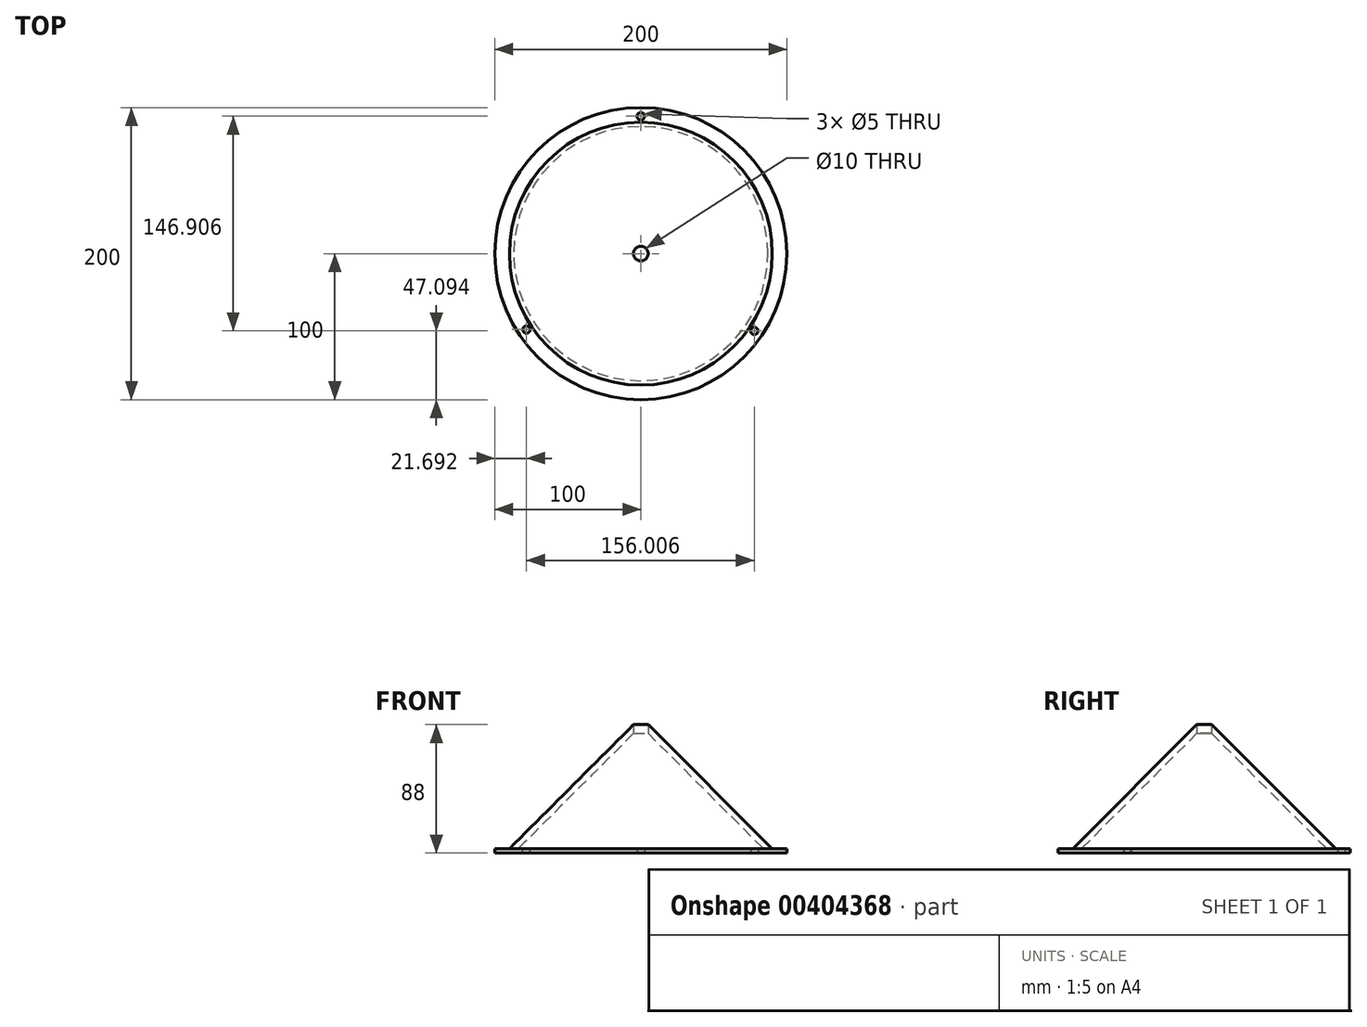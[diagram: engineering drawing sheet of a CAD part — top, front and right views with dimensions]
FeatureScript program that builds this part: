
annotation { "Feature Type Name" : "Feature", "Feature Type Description" : "" }
export const myFeature = defineFeature(function(context is Context, id is Id, definition is map)
    precondition{}
    {
        {
            var Q0;
            Q0=qCreatedBy(makeId("Front.planeOp"),FACE);
            var sketch = newSketch(context, id + "F0", { "sketchPlane" : qUnion([Q0])});
            skLineSegment(sketch, "E0", {"start": v(0, 0) * mm, "end": v(-100, 0) * mm});
            skLineSegment(sketch, "E1", {"start": v(-100, 0) * mm, "end": v(-100, 3) * mm});
            skLineSegment(sketch, "E2", {"start": v(-100, 3) * mm, "end": v(-90, 3) * mm});
            skLineSegment(sketch, "E3", {"start": v(-90, 3) * mm, "end": v(0, 93) * mm});
            skLineSegment(sketch, "E4", {"start": v(0, 93) * mm, "end": v(0, 0) * mm});
            skSolve(sketch);
        }
        {
            var Q0;
            Q0=makeQuery(id+"F0.imprint","IMPRINT",FACE,{"disambiguationData":[TD([[makeQuery(id+"F0.imprint","IMPRINT",EDGE,{"derivedFrom":sQuery(id+"F0.wireOp",EDGE,"E0")}),-1.0]])]});
            var Q1;
            Q1=sQuery(id+"F0.wireOp",EDGE,"E4");
            revolve(context, id + "F1", {"entities" : qUnion([Q0]), "axis" : qUnion([Q1]), "revolveType" : RevolveType.FULL});
        }
        {
            var Q0;
            Q0=makeQuery(id+"F1.opRevolve","SWEPT_FACE",FACE,{"disambiguationData":[OSD([sQuery(id+"F0.wireOp",EDGE,"E0")])]});
            var sketch = newSketch(context, id + "F2", { "sketchPlane" : qUnion([Q0])});
            skCircle(sketch, "E5", {"center": v(0, 0) * mm, "radius": 87 * mm});
            skSolve(sketch);
        }
        {
            var Q0;
            Q0=makeQuery(id+"F2.imprint","IMPRINT",FACE,{"disambiguationData":[TD([[makeQuery(id+"F2.imprint","IMPRINT",EDGE,{"derivedFrom":sQuery(id+"F2.wireOp",EDGE,"E5")}),1.0]])]});
            extrude(context, id + "F3", {"entities" : qUnion([Q0]), "operationType" : NewBodyOperationType.REMOVE, "endBound" : BoundingType.THROUGH_ALL, "oppositeDirection" : true, "depth" : 25 * mm, "hasDraft" : true, "draftAngle" : 45 * degree, "draftPullDirection" : true});
        }
        {
            var Q0;
            Q0=qCreatedBy(makeId("Top.planeOp"),FACE);
            var sketch = newSketch(context, id + "F4", { "sketchPlane" : qUnion([Q0])});
            skCircle(sketch, "E6", {"center": v(0, 0) * mm, "radius": 5 * mm});
            skSolve(sketch);
        }
        {
            var Q0;
            Q0=makeQuery(id+"F4.imprint","IMPRINT",FACE,{"disambiguationData":[TD([[makeQuery(id+"F4.imprint","IMPRINT",EDGE,{"derivedFrom":sQuery(id+"F4.wireOp",EDGE,"E6")}),1.0]])]});
            extrude(context, id + "F5", {"entities" : qUnion([Q0]), "operationType" : NewBodyOperationType.REMOVE, "endBound" : BoundingType.THROUGH_ALL, "depth" : 25 * mm});
        }
        {
            var Q0;
            Q0=makeQuery(id+"F1.opRevolve","SWEPT_FACE",FACE,{"disambiguationData":[OSD([sQuery(id+"F0.wireOp",EDGE,"E2")])]});
            var sketch = newSketch(context, id + "F6", { "sketchPlane" : qUnion([Q0])});
            skCircle(sketch, "E7", {"center": v(0, 94) * mm, "radius": 2.5 * mm});
            skCircle(sketch, "E8", {"center": v(81.34, -47.1) * mm, "radius": 2.5 * mm});
            skCircle(sketch, "E9", {"center": v(-80.64, -48.3) * mm, "radius": 2.5 * mm});
            skSolve(sketch);
        }
        {
            var Q0;
            Q0=makeQuery(id+"F6.imprint","IMPRINT",FACE,{"disambiguationData":[TD([[makeQuery(id+"F6.imprint","IMPRINT",EDGE,{"derivedFrom":sQuery(id+"F6.wireOp",EDGE,"E7")}),1.0]])]});
            extrude(context, id + "F7", {"entities" : qUnion([Q0]), "operationType" : NewBodyOperationType.REMOVE, "endBound" : BoundingType.SYMMETRIC, "depth" : 25 * mm});
        }
        {
            var Q0;
            Q0=makeQuery(id+"F1.opRevolve","SWEPT_FACE",FACE,{"disambiguationData":[OSD([sQuery(id+"F0.wireOp",EDGE,"E0")])]});
            var sketch = newSketch(context, id + "F8", { "sketchPlane" : qUnion([Q0])});
            skCircle(sketch, "E10", {"center": v(-78.3, 52) * mm, "radius": 2.5 * mm});
            skSolve(sketch);
        }
        {
            var Q0;
            Q0=makeQuery(id+"F8.imprint","IMPRINT",FACE,{"disambiguationData":[TD([[makeQuery(id+"F8.imprint","IMPRINT",EDGE,{"derivedFrom":sQuery(id+"F8.wireOp",EDGE,"E10")}),1.0]])]});
            extrude(context, id + "F9", {"entities" : qUnion([Q0]), "operationType" : NewBodyOperationType.REMOVE, "endBound" : BoundingType.SYMMETRIC, "depth" : 25 * mm});
        }
        {
            var Q0;
            Q0=makeQuery(id+"F1.opRevolve","SWEPT_FACE",FACE,{"disambiguationData":[OSD([sQuery(id+"F0.wireOp",EDGE,"E0")])]});
            var sketch = newSketch(context, id + "F10", { "sketchPlane" : qUnion([Q0])});
            skCircle(sketch, "E11", {"center": v(77.7, 52.9) * mm, "radius": 2.5 * mm});
            skSolve(sketch);
        }
        {
            var Q0;
            Q0=makeQuery(id+"F10.imprint","IMPRINT",FACE,{"disambiguationData":[TD([[makeQuery(id+"F10.imprint","IMPRINT",EDGE,{"derivedFrom":sQuery(id+"F10.wireOp",EDGE,"E11")}),1.0]])]});
            extrude(context, id + "F11", {"entities" : qUnion([Q0]), "operationType" : NewBodyOperationType.REMOVE, "endBound" : BoundingType.SYMMETRIC, "oppositeDirection" : true, "depth" : 25 * mm});
        }
    });
